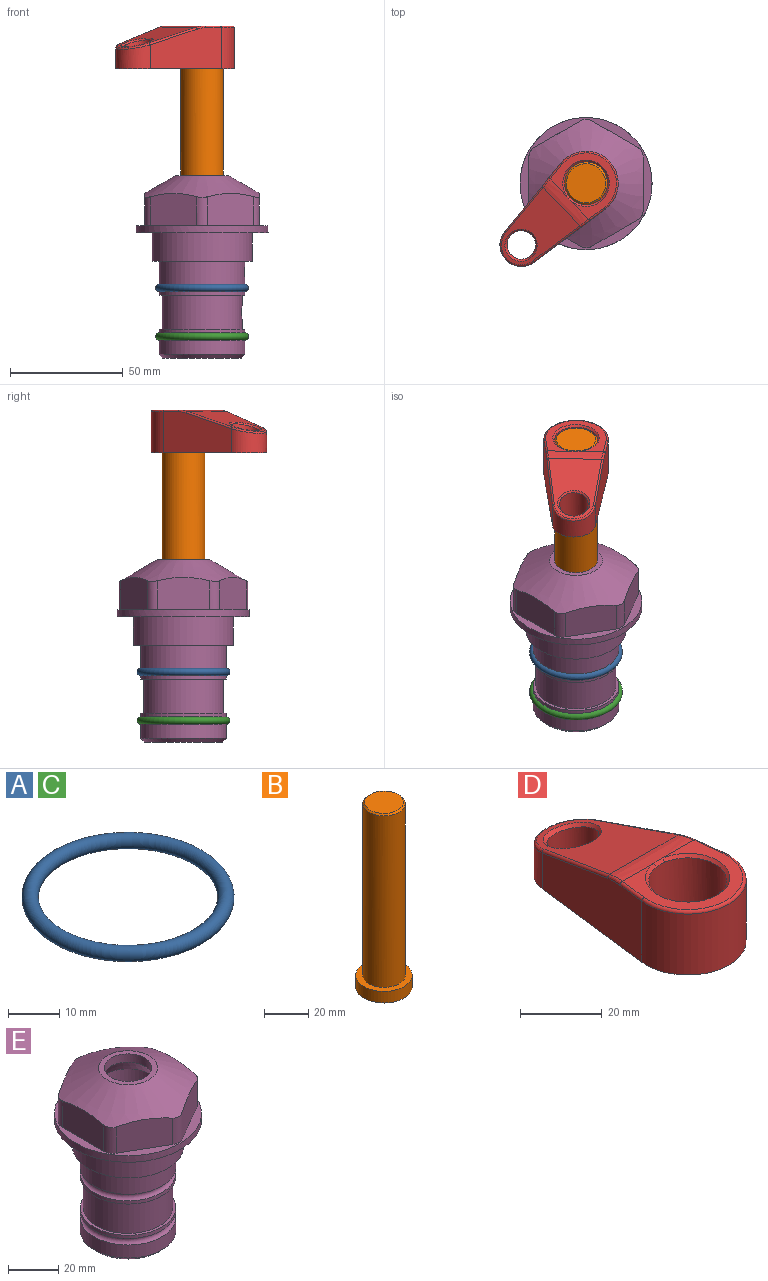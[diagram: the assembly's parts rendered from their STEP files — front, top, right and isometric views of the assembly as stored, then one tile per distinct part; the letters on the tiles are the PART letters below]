
ASSEMBLY  parts=5 mates=4
PART A: 1 faces, bbox 44.7x44.7x3.2 mm
  f0: torus R=19.05mm, axis (0,0,1), area 1193.9mm2
PART B: 6 faces, bbox 25.4x25.4x101.6 mm
  f0: plane 17.46x17.46mm, normal (0,0,1), area 239.5mm2, adj f5
  f1: plane 25.4x25.4mm, normal (0,0,-1), area 506.7mm2, adj f2
  f2: cylinder r=12.7mm len=25.4mm, axis (0,0,1), area 506.7mm2, adj f1,f3
  f3: plane 25.4x25.4mm, normal (0,0,1), area 221.7mm2, adj f2,f4
  f4: cylinder r=9.53mm len=94.46mm, axis (0,0,1), area 5653mm2, adj f3,f5
  f5: cone r=8.73mm half-angle=45deg, axis (0,0,-1), area 64.4mm2, adj f0,f4
PART C: same geometry as A
PART D: 31 faces, bbox 31.7x65.5x19.8 mm
  f0: plane 39.12x18.26mm, normal (0.99,0.12,0), area 612.2mm2, adj f1,f4,f7,f11,f13,f15
  f1: cylinder r=9.53mm len=18.91mm, axis (0,0,-1), area 296.1mm2, adj f0,f2,f7,f17
  f2: plane 39.12x18.26mm, normal (-0.99,0.12,0), area 612.2mm2, adj f1,f4,f7,f12,f14,f16
  f3: cylinder r=6.35mm len=12.7mm, axis (0,0,-1), area 362.4mm2, adj f7,f18
  f4: cylinder r=14.29mm len=28.58mm, axis (0,0,-1), area 882.2mm2, adj f0,f2,f7,f10
  f5: cylinder r=9.53mm len=19.05mm, axis (0,0,-1), area 1092.6mm2, adj f7,f19,f20
  f6: plane 26.99x23.69mm, normal (0,0,1), area 216.2mm2, adj f9,f10,f11,f12,f19
  f7: plane 63.5x28.58mm, normal (0,0,-1), area 661.8mm2, adj f0,f1,f2,f3,f4,f5,f22,f23
  f8: plane 33.52x23.6mm, normal (0,0.26,0.97), area 486mm2, adj f9,f15,f16,f17,f18
  f9: cylinder r=19.05mm len=24.72mm, axis (1,0,0), area 120.4mm2, adj f6,f8,f13,f14,f20
  f10: torus R=13.49mm, axis (0,0,1), area 59mm2, adj f4,f6,f11,f12
  f11: cylinder r=0.79mm len=8.67mm, axis (0.12,-0.99,0), area 10.8mm2, adj f0,f6,f10,f13
  f12: cylinder r=0.79mm len=8.67mm, axis (0.12,0.99,0), area 10.8mm2, adj f2,f6,f10,f14
  f13: bspline ~4.95x1.42mm, area 6.1mm2, adj f0,f9,f11,f15
  f14: bspline ~4.95x1.42mm, area 6.1mm2, adj f2,f9,f12,f16
  f15: cylinder r=0.79mm len=25.95mm, axis (0.12,-0.96,0.26), area 32.9mm2, adj f0,f8,f13,f17
  f16: cylinder r=0.79mm len=25.95mm, axis (0.12,0.96,-0.26), area 32.9mm2, adj f2,f8,f14,f17
  f17: bspline ~18.91x8.38mm, area 30mm2, adj f1,f8,f15,f16
  f18: bspline ~14.29x14.29mm, area 48.3mm2, adj f3,f8
  f19: cone r=9.53mm half-angle=45deg, axis (0,0,1), area 66.5mm2, adj f5,f6,f20
  f20: bspline ~3.22x0.96mm, area 3.5mm2, adj f5,f9,f19
  f21: plane 2.75x2.72mm, normal (0,0,-1), area 2.9mm2, adj f23,f25,f28
  f22: plane 23.05x15.88mm, normal (-0.99,-0.12,0), area 323.6mm2, adj f7,f25,f26,f27,f28,f29
  f23: plane 23.05x15.88mm, normal (0.99,-0.12,0), area 323.6mm2, adj f7,f21,f25,f27,f28,f30
  f24: cylinder r=9.53mm len=10.69mm, axis (0,0,-1), area 114.7mm2, adj f7,f27,f29,f30
  f25: cylinder r=12.7mm len=20.59mm, axis (0,0,-1), area 381.1mm2, adj f7,f21,f22,f23,f26,f28
  f26: plane 2.75x2.72mm, normal (0,0,-1), area 2.9mm2, adj f22,f25,f28
  f27: plane 19.72x18.37mm, normal (0,-0.26,-0.97), area 291.8mm2, adj f22,f23,f24,f28,f29,f30
  f28: cylinder r=15.88mm len=19.92mm, axis (1,0,0), area 54.8mm2, adj f21,f22,f23,f25,f26,f27
  f29: cylinder r=1.59mm len=11mm, axis (0,0,-1), area 34.7mm2, adj f7,f22,f24,f27
  f30: cylinder r=1.59mm len=11mm, axis (0,0,-1), area 34.7mm2, adj f7,f23,f24,f27
PART E: 36 faces, bbox 58.7x58.7x81 mm
  f0: cylinder r=17.78mm len=35.56mm, axis (0,0,1), area 1670.8mm2, adj f23,f24,f31
  f1: cylinder r=19.05mm len=38.1mm, axis (0,0,1), area 1191.9mm2, adj f26,f27,f30
  f2: plane 58.66x58.66mm, normal (0,0,-1), area 1150.6mm2, adj f3,f28
  f3: cylinder r=29.33mm len=58.66mm, axis (0,0,-1), area 585.1mm2, adj f2,f4
  f4: plane 58.66x58.66mm, normal (0,0,1), area 475.9mm2, adj f3,f5,f6,f7,f8,f9,f10,f11
  f5: plane 20.32x14.34mm, normal (-0.5,0.87,0), area 324.4mm2, adj f4,f15,f16,f17
  f6: plane 20.32x14.34mm, normal (0.5,0.87,0), area 324.4mm2, adj f4,f14,f15,f17
  f7: plane 23.48x14.34mm, normal (1,0,0), area 324.4mm2, adj f4,f13,f14,f17
  f8: plane 20.32x14.34mm, normal (0.5,-0.87,0), area 324.4mm2, adj f4,f12,f13,f17
  f9: plane 20.32x14.34mm, normal (-0.5,-0.87,0), area 324.4mm2, adj f4,f11,f12,f17
  f10: plane 23.48x14.34mm, normal (-1,0,0), area 324.4mm2, adj f4,f11,f16,f17
  f11: cylinder r=5.08mm len=12.85mm, axis (0,0,-1), area 67.2mm2, adj f4,f9,f10,f17
  f12: cylinder r=5.08mm len=12.85mm, axis (0,0,-1), area 67.2mm2, adj f4,f8,f9,f17
  f13: cylinder r=5.08mm len=12.85mm, axis (0,0,-1), area 67.2mm2, adj f4,f7,f8,f17
  f14: cylinder r=5.08mm len=12.85mm, axis (0,0,-1), area 67.2mm2, adj f4,f6,f7,f17
  f15: cylinder r=5.08mm len=12.85mm, axis (0,0,-1), area 67.2mm2, adj f4,f5,f6,f17
  f16: cylinder r=5.08mm len=12.85mm, axis (0,0,-1), area 67.2mm2, adj f4,f5,f10,f17
  f17: cone r=11.73mm half-angle=60deg, axis (0,0,-1), area 2071.8mm2, adj f5,f6,f7,f8,f9,f10,f11,f12
  f18: plane 23.46x23.46mm, normal (0,0,1), area 147.4mm2, adj f17,f35
  f19: plane 34.93x34.93mm, normal (0,0,-1), area 958mm2, adj f29
  f20: cylinder r=19.05mm len=38.1mm, axis (0,0,1), area 760.1mm2, adj f21,f29
  f21: torus R=19.05mm, axis (0,0,1), area 565.3mm2, adj f20,f22
  f22: cylinder r=19.05mm len=38.1mm, axis (0,0,1), area 190mm2, adj f21,f23
  f23: plane 38.1x38.1mm, normal (0,0,1), area 146.9mm2, adj f0,f22
  f24: plane 38.1x38.1mm, normal (0,0,-1), area 146.9mm2, adj f0,f25
  f25: cylinder r=19.05mm len=38.1mm, axis (0,0,1), area 190mm2, adj f24,f26
  f26: torus R=19.05mm, axis (0,0,1), area 565.3mm2, adj f1,f25
  f27: plane 44.45x44.45mm, normal (0,0,-1), area 411.7mm2, adj f1,f28
  f28: cylinder r=22.23mm len=44.45mm, axis (0,0,1), area 1773.5mm2, adj f2,f27
  f29: cone r=19.05mm half-angle=45deg, axis (0,0,1), area 257.5mm2, adj f19,f20
  f30: cylinder r=3.17mm len=6.75mm, axis (-1,0,0), area 128mm2, adj f1,f33
  f31: cylinder r=3.17mm len=6.35mm, axis (-1,0,0), area 102.5mm2, adj f0,f33
  f32: plane 25.4x25.4mm, normal (0,0,1), area 506.7mm2, adj f33
  f33: cylinder r=12.7mm len=66.42mm, axis (0,0,-1), area 5236.2mm2, adj f30,f31,f32,f34
  f34: cone r=9.53mm half-angle=30deg, axis (0,0,-1), area 443.4mm2, adj f33,f35
  f35: cylinder r=9.53mm len=19.05mm, axis (0,0,-1), area 240.9mm2, adj f18,f34
PLACE A at identity
PLACE B rot(axis=(0,0,1),133.6deg) t=(0,0,27.55)mm
PLACE C t=(0,0,-21.59)mm
PLACE D rot(axis=(0,0,1),133.6deg) t=(0,0,28.35)mm
PLACE E at identity fixed
MATE fastened B.f2 <-> D.f4  axis (0,0,1) through (0,0,91.05)mm
MATE fastened C.f0 <-> E.f0  axis (0,0,1) through (0,0,-46.1)mm
MATE cylindrical B.f2 <-> E.f0  axis (0,0,-1) through (0,0,-10.55)mm
MATE fastened A.f0 <-> E.f0  axis (0,0,1) through (0,0,-24.51)mm
